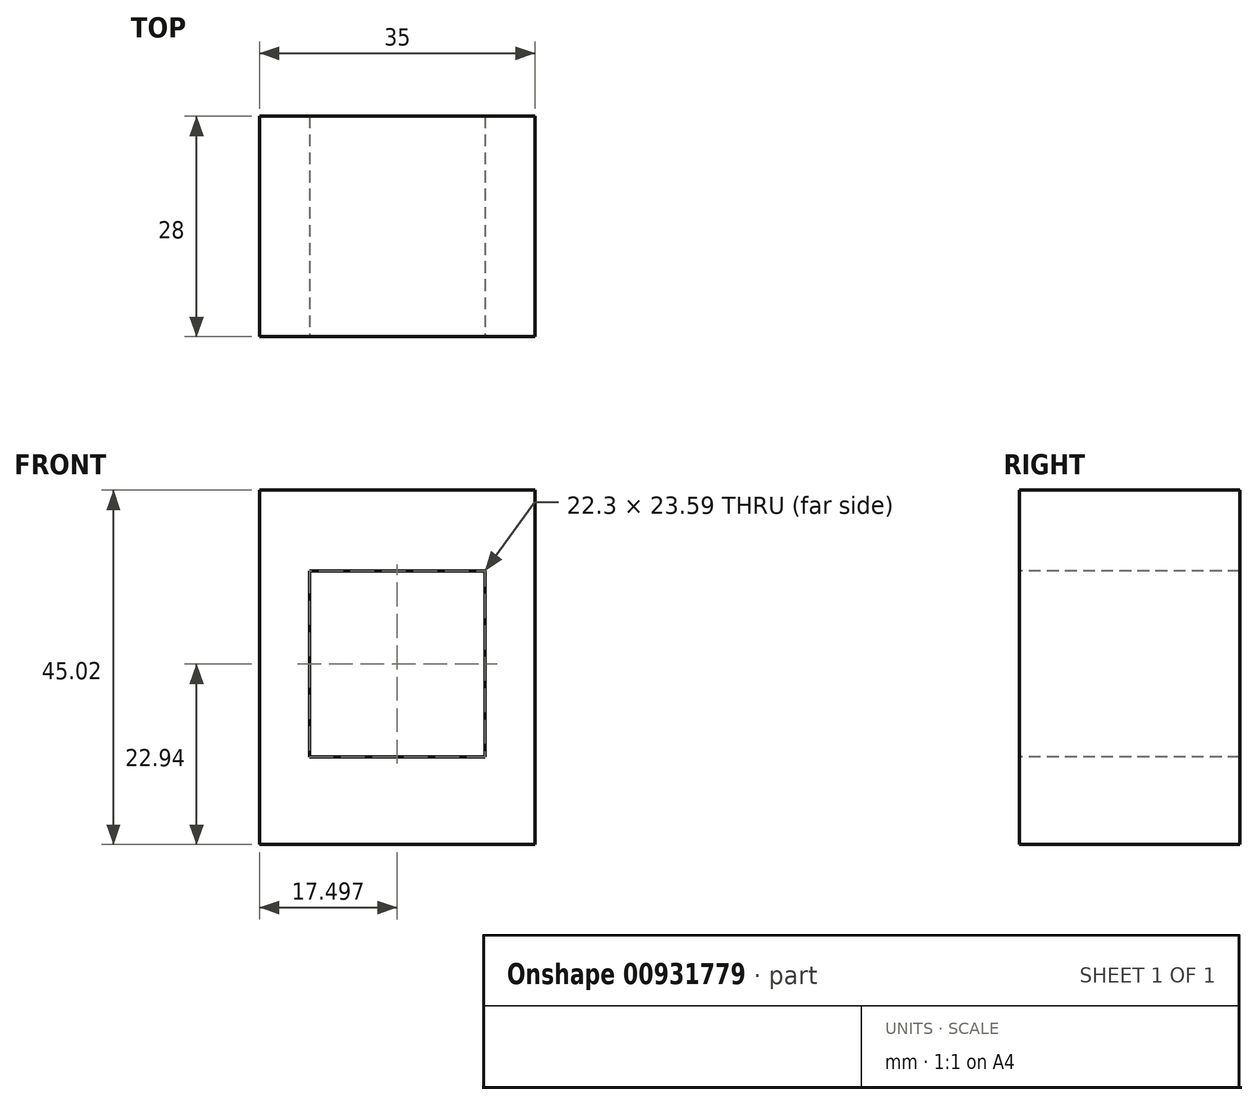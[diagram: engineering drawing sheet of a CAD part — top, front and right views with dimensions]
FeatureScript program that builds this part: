
annotation { "Feature Type Name" : "Feature", "Feature Type Description" : "" }
export const myFeature = defineFeature(function(context is Context, id is Id, definition is map)
    precondition{}
    {
        {
            var Q0;
            Q0=qCreatedBy(makeId("Top.planeOp"),FACE);
            var sketch = newSketch(context, id + "F0", { "sketchPlane" : qUnion([Q0])});
            skLineSegment(sketch, "E0.bottom", {"start": v(12.24, -15.44) * mm, "end": v(-22.76, -15.44) * mm});
            skLineSegment(sketch, "E0.top", {"start": v(12.24, 12.56) * mm, "end": v(-22.76, 12.56) * mm});
            skLineSegment(sketch, "E0.left", {"start": v(12.24, -15.44) * mm, "end": v(12.24, 12.56) * mm});
            skLineSegment(sketch, "E0.right", {"start": v(-22.76, -15.44) * mm, "end": v(-22.76, 12.56) * mm});
            skSolve(sketch);
        }
        {
            var Q0;
            Q0=makeQuery(id+"F0.imprint","IMPRINT",FACE,{"disambiguationData":[TD([[makeQuery(id+"F0.imprint","IMPRINT",EDGE,{"derivedFrom":sQuery(id+"F0.wireOp",EDGE,"E0.bottom")}),-1.0]])]});
            var sketch = newSketch(context, id + "F1", { "sketchPlane" : qUnion([Q0])});
            skSolve(sketch);
        }
        {
            var Q0;
            Q0=makeQuery(id+"F1.imprint","IMPRINT",FACE,{"disambiguationData":[TD([[makeQuery(id+"F1.imprint","IMPRINT",EDGE,{"derivedFrom":makeQuery(id+"F0.imprint","IMPRINT",EDGE,{"derivedFrom":sQuery(id+"F0.wireOp",EDGE,"E0.bottom")})}),-1.0]])]});
            extrude(context, id + "F2", {"entities" : qUnion([Q0]), "depth" : 45.02 * mm, "offsetDistance" : 25.4 * mm});
        }
        {
            var Q0;
            Q0=makeQuery(id+"F2.opExtrude","SWEPT_FACE",FACE,{"disambiguationData":[OSD([sQuery(id+"F0.wireOp",EDGE,"E0.bottom")])]});
            var sketch = newSketch(context, id + "F3", { "sketchPlane" : qUnion([Q0])});
            skLineSegment(sketch, "E1.bottom", {"start": v(5.89, 11.14) * mm, "end": v(-16.41, 11.14) * mm});
            skLineSegment(sketch, "E1.top", {"start": v(5.89, 34.73) * mm, "end": v(-16.41, 34.73) * mm});
            skLineSegment(sketch, "E1.left", {"start": v(5.89, 11.14) * mm, "end": v(5.89, 34.73) * mm});
            skLineSegment(sketch, "E1.right", {"start": v(-16.41, 11.14) * mm, "end": v(-16.41, 34.73) * mm});
            skSolve(sketch);
        }
        {
            var Q0;
            Q0=makeQuery(id+"F3.imprint","IMPRINT",FACE,{"disambiguationData":[TD([[makeQuery(id+"F3.imprint","IMPRINT",EDGE,{"derivedFrom":sQuery(id+"F3.wireOp",EDGE,"E1.bottom")}),-1.0]])]});
            extrude(context, id + "F4", {"entities" : qUnion([Q0]), "operationType" : NewBodyOperationType.REMOVE, "endBound" : BoundingType.THROUGH_ALL, "oppositeDirection" : true, "depth" : 25.4 * mm, "offsetDistance" : 25.4 * mm});
        }
    });
